# Revit family: 0060798 Sylvania Lighting Fixture FREEOFFICE DIRECT INDIRECT 14KLM PIR WHITE EC
name_source: partatom
category: Lighting Fixtures
revit_build: Autodesk Revit 2016 (Build: 20150220_1215(x64)
units: mm (PartAtom-declared; Revit-internal decimal feet)

## family parameters
Cut with Voids When Loaded = No
Host = Face
Light Source = Yes
OmniClass Number = 23.80.70.11.17
OmniClass Title = Specialized Lighting by Location or Use
Part Type = Normal
Room Calculation Point = No
Round Connector Dimension = Use Diameter
Shared = No

## types (1)
- 0060798 FREEOFFICE D/I 14 PIR WHITE EC
    Apparent Load = 107 VA
    Assembly Code = D5020200
    AssetType = Fixed
    Color Filter = 16777215
    Default Elevation = 0 mm  [stored 0 ft]
    Description = FREEOFFICE DIRECT/INDIRECT 14KLM PIR WHITE EC is a highly efficient free-standing floor lamp providing optimal illumination for single and twin workstations. 80% uplight and 20% downlight ratio for ambient and task lighting from a single luminaire. Microprismatic PMMA optics for advanced glare control. White RAL9010 powder coated luminaire body. Aluminium head and pole for high-quality appearance, steel stand for higher stability. Luminaire dimensions: Head: 690x397x25mm, Stand: 480x460x16mm, Pole: 55x35x2030mm. Operated and dimmed with a push button located in the pole at a height suitable to be used with adjustable height desks. Equipped with presence and daylight sensor. Up and downlight dims together. 4000K Neutral White LED, CRI>80, chromaticity tolerance: SDCM<3. Luminous flux: 14100lm. Power consumption 107W. Luminaire efficacy: 132lm/W. Lumen maintenance: L80B50=55000h. UGR<16, Luminance at 65°<3000 cd/m2. IK02, IP20. Photobiological safety risk group 0. Electrical protection: Class I. Glow wire test: 650°C. Supplied with 3m cable with DIN 49441-R2 plug.
    Diameter_FEILO = 330 mm
    Dimming Lamp Color Temperature Shift = <None>
    DimmingControlOptions = Dimmable
    DocumentationLiterature = http://www.sylvania-lighting.com
    DurationUnit = hours
    ElectricShockClassification = Class I
    Emit Shape Visible in Rendering = No
    Emit from Rectangle Length = 564.6 mm  [stored 1.85236 ft]
    Emit from Rectangle Width = 340.1 mm  [stored 1.11581 ft]
    ExpectedLife = 50000
    Height_FEILO = 96 mm  [stored 0.314961 ft]
    IfcExportAs = IfcLightFixtureType
    IfcExportType = IfcLightFixtureType
    ImpactProtectionIndex = IK02
    IngressProtection = IP20
    InputNominalFrequency = 50/60 Hz
    InputVoltage = 220-240V~
    Keynote = 16500
    Lamp = LED
    LampColourRenderingIndex = 80
    LampColourTemperature = 4000 K
    LampMacAdamStep = 3
    LampNominalLuminous = 14100 lm
    LampsType = LED
    LuminousEfficacy = 132 lm/W
    Manufacturer = Feilo Sylvania
    ManufacturerName = Feilo Sylvania
    Material = head and pole : powder coated aluminium. stand: powder coated steel housing, pmma diffuser
    Material_1_SYL = Body-Sylvania-FreeOffice-WH
    Material_2_SYL = Polycarbonate_Sylvania_Sylcircle_Opal
    Material_3_SYL = Body-Sylvania-FreeOffice-BLK
    Model = FREEOFFICE DIRECT/INDIRECT 14KLM PIR WHITE EC
    ModelNumber = 0060798
    ModelReference = FREEOFFICE DIRECT/INDIRECT 14KLM PIR WHITE EC
    Name = FREEOFFICE DIRECT/INDIRECT 14KLM PIR WHITE EC
    NominalHeight = 2030 mm  [stored 6.6601 ft]
    NominalLength = 690 mm  [stored 2.26378 ft]
    NominalWidth = 0 mm  [stored 0 ft]
    PIR_SYL = Yes
    Photometric Web File = 0060798.ies
    PowerConsumption = 107 W
    PowerFactor = 0.98
    Radius_FEILO = 165 mm
    Tilt Angle = -90°
    TypeName = FREEOFFICE DIRECT/INDIRECT 14KLM PIR WHITE EC
    URL = http://www.sylvania-lighting.com
    Voltage = 230 V
    Weight = 22.8 kg

note: [stored X ft] marks values corroborated as IEEE doubles in the binary element streams (Revit-internal decimal feet)

## geometry (parser evidence)
native form markers: Sweep x1
no freeform markers — native parametric forms only
